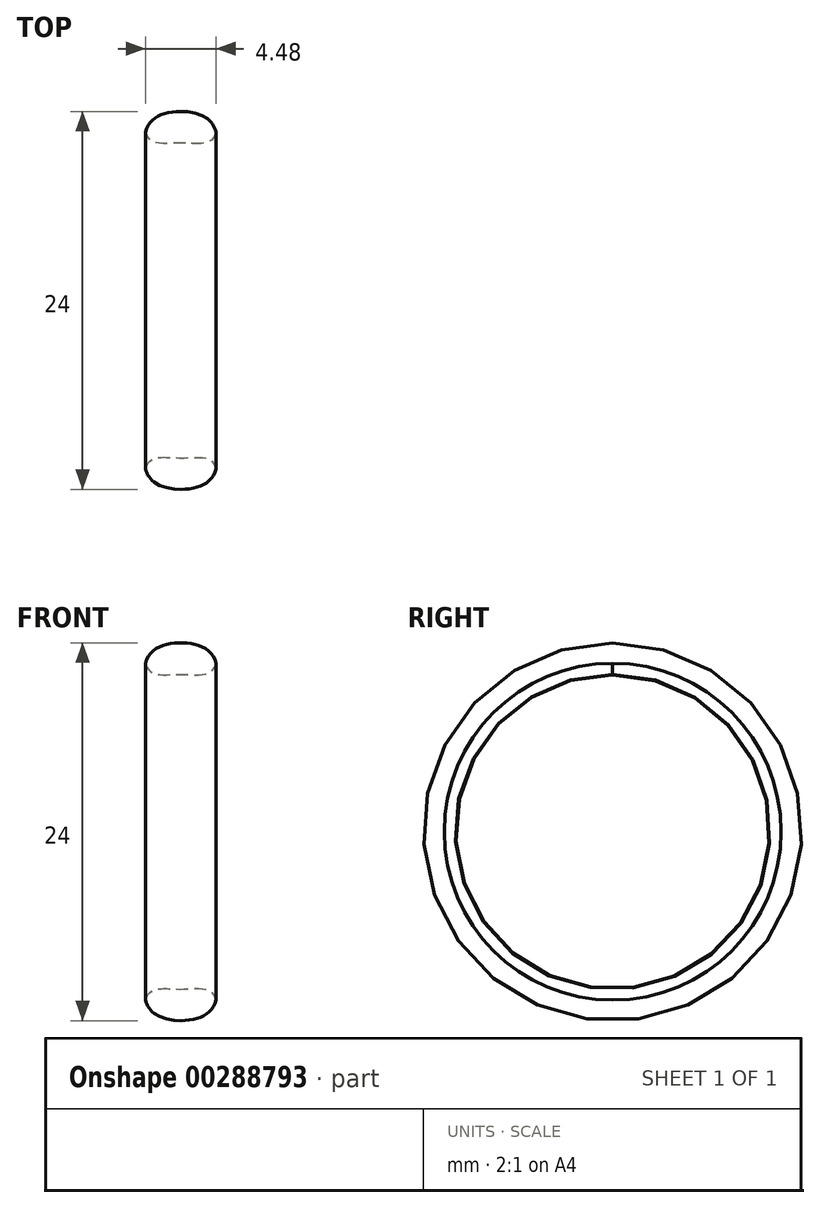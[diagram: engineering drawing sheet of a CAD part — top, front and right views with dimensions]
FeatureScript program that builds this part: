
annotation { "Feature Type Name" : "Feature", "Feature Type Description" : "" }
export const myFeature = defineFeature(function(context is Context, id is Id, definition is map)
    precondition{}
    {
        {
            var Q0;
            Q0=qCreatedBy(makeId("Front.planeOp"),FACE);
            var sketch = newSketch(context, id + "F0", { "sketchPlane" : qUnion([Q0])});
            skFitSpline(sketch, "E0", {"points": [v(-2.24, 0) * mm, v(0, 1.3) * mm, v(2.24, 0) * mm], "startDerivative": vector(1.34, 5.84) * mm, "endDerivative": vector(1.34, -5.84) * mm});
            skFitSpline(sketch, "E1", {"points": [v(-2.24, 0) * mm, v(0, -0.7) * mm, v(2.24, 0) * mm], "startDerivative": vector(1.34, -5.84) * mm, "endDerivative": vector(1.34, 5.84) * mm});
            skLineSegment(sketch, "E2", {"start": v(0, -1.76) * mm, "end": v(0, -10.7) * mm, "construction": true});
            skLineSegment(sketch, "E3", {"start": v(0, -10.7) * mm, "end": v(8.85, -10.7) * mm, "construction": true});
            skSolve(sketch);
        }
        {
            var Q0;
            Q0=makeQuery(id+"F0.imprint","IMPRINT",FACE,{"disambiguationData":[TD([[makeQuery(id+"F0.imprint","IMPRINT",EDGE,{"derivedFrom":sQuery(id+"F0.wireOp",EDGE,"E0")}),-1.0]])]});
            var Q1;
            Q1=sQuery(id+"F0.wireOp",EDGE,"E2");
            var Q2;
            Q2=sQuery(id+"F0.wireOp",EDGE,"E3");
            var Q3;
            Q3=sQuery(id+"F0.wireOp",EDGE,"E3");
            revolve(context, id + "F1", {"entities" : qUnion([Q0]), "surfaceEntities" : qUnion([Q1, Q2]), "axis" : qUnion([Q3]), "revolveType" : RevolveType.FULL, "surfaceOperationType" : NewSurfaceOperationType.NEW});
        }
    });
